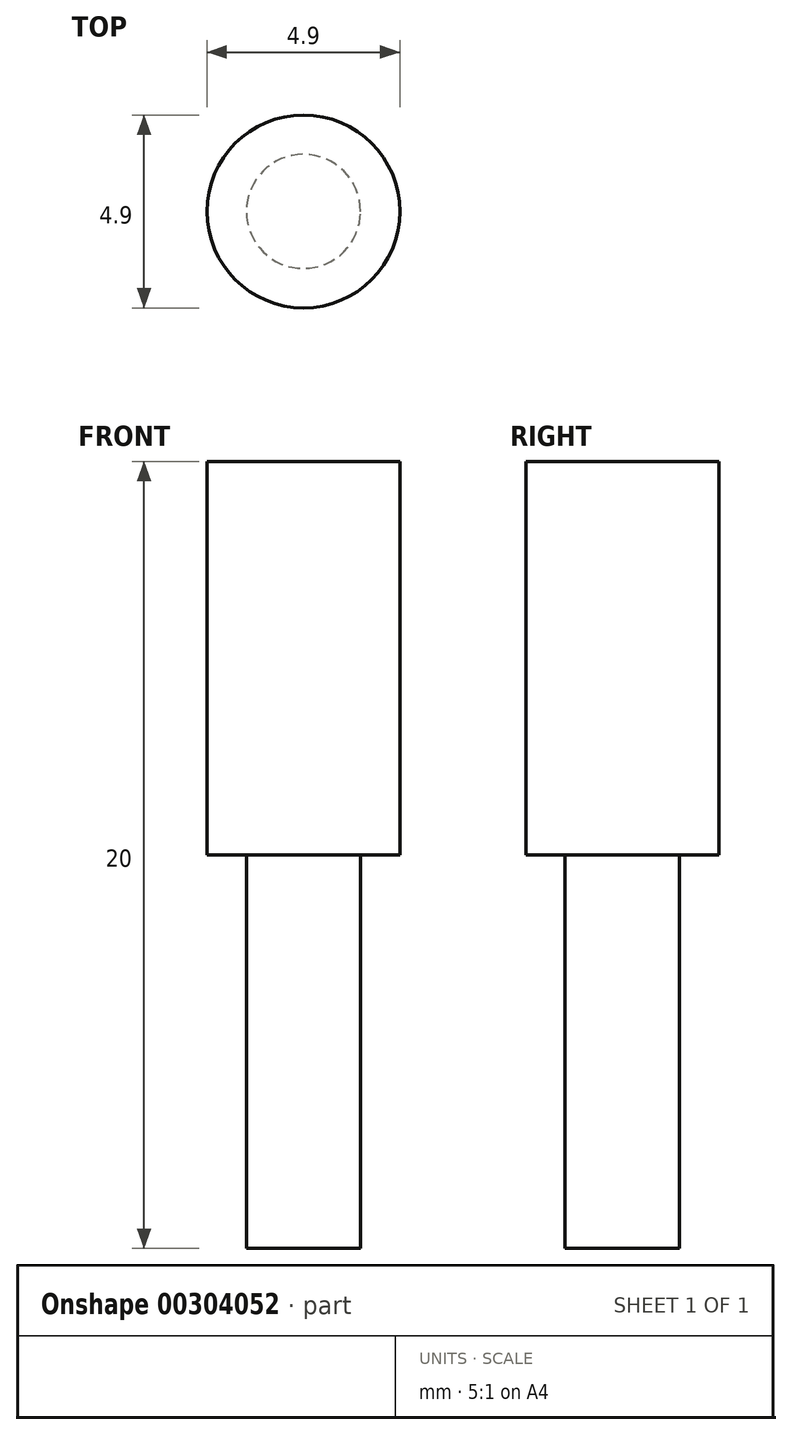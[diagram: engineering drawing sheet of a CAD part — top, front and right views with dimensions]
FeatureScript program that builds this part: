
annotation { "Feature Type Name" : "Feature", "Feature Type Description" : "" }
export const myFeature = defineFeature(function(context is Context, id is Id, definition is map)
    precondition{}
    {
        {
            var Q0;
            Q0=qCreatedBy(makeId("Top.planeOp"),FACE);
            var sketch = newSketch(context, id + "F0", { "sketchPlane" : qUnion([Q0])});
            skCircle(sketch, "E0", {"center": v(0, 0) * mm, "radius": 2.45 * mm});
            skCircle(sketch, "E1", {"center": v(0, 0) * mm, "radius": 1.5 * mm});
            skSolve(sketch);
        }
        {
            var Q0;
            Q0=makeQuery(id+"F0.imprint","IMPRINT",FACE,{"disambiguationData":[TD([[makeQuery(id+"F0.imprint","IMPRINT",EDGE,{"derivedFrom":sQuery(id+"F0.wireOp",EDGE,"E1")}),1.0]])]});
            var Q1;
            Q1=makeQuery(id+"F0.imprint","IMPRINT",FACE,{"disambiguationData":[TD([[makeQuery(id+"F0.imprint","IMPRINT",EDGE,{"derivedFrom":sQuery(id+"F0.wireOp",EDGE,"E0")}),1.0]])]});
            extrude(context, id + "F1", {"entities" : qUnion([Q0, Q1]), "depth" : 10 * mm});
        }
        {
            var Q0;
            Q0=makeQuery(id+"F1.opExtrude","CAP_FACE",FACE,{"disambiguationData":[OSD([sQuery(id+"F0.wireOp",EDGE,"E0")])],"isStart":true});
            var sketch = newSketch(context, id + "F2", { "sketchPlane" : qUnion([Q0])});
            skCircle(sketch, "E2", {"center": v(0, 0) * mm, "radius": 1.45 * mm});
            skSolve(sketch);
        }
        {
            var Q0;
            Q0=makeQuery(id+"F2.imprint","IMPRINT",FACE,{"disambiguationData":[TD([[makeQuery(id+"F2.imprint","IMPRINT",EDGE,{"derivedFrom":sQuery(id+"F2.wireOp",EDGE,"E2")}),1.0]])]});
            extrude(context, id + "F3", {"entities" : qUnion([Q0]), "operationType" : NewBodyOperationType.ADD, "depth" : 10 * mm});
        }
    });
